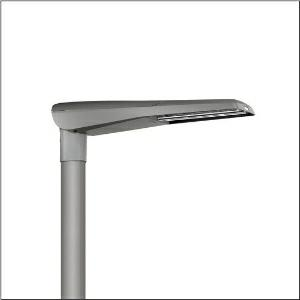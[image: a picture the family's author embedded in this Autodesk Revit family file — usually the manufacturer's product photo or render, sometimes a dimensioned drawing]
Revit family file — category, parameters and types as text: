
# Revit family: streetlight_sl_11_iq_mini___st0_5st0_5_5xc2hc1f08ge_9336
name_source: partatom
category: Lighting Fixtures
units: mm (PartAtom-declared; Revit-internal decimal feet)

## family parameters
Cut with Voids When Loaded = No
Host = Face
Light Source = No
Part Type = Normal
Room Calculation Point = No
Round Connector Dimension = Use Diameter
Shared = No

## types (1)
- --- (1 x LED, 3020 lm, 25.3 W, 2200K)
    Apparent Load = 25 VA
    CIE Flux Codes = 43 74 97 100 100
    Color Rendering = 70
    Color Temperature = 2200K
    Default Elevation = 1800 mm
    Description = Streetlight SL 11 iQ mini, mast luminaire, primary light control with 3 zone facetted reflector, of plastic, silver coated, highly specular, primary optical cover: cover, of PMMA, transparent, light distribution: ST0.5ST0.5, light emission: direct distribution, primary light characteristic: asymmetric, installation type: post-top, side-entry, lamps: LED, High Power LED, rated values: 3.550lm | 24,9W | 142,6lm/W (begin service life); end service life: 3.550lm | 25,7W; at 50% lumin. flux: 1.775lm | 12,8W | 138,7lm/W, colour temperature: 2200/2700/3000/4000K, colour rendering: CRI > 70, light colour: 722/727/730/740, light setting 1 begin service life: 100% | 3.550lm | 24,9W | 142,6lm/W | 3.000K, light setting 1 end service life: 25,7W, further light settings possible, control: Street-Remote, Auto-Match, Temp-Guard, Lumen-Switch, Night-Set, Smart-Wire, Light-Fading, Desk-Remote (wireless, voltage-free reading and setting of iQ features in the workshop via application-optimized NFC function/RFID function), optimised constant luminous flux control (CLO 2.0), with cable H07RN-F 5x 1.5mm², mains connection: 230..240V, AC, 50/60Hz, connection cable pre-assembled, cable length: 6,5m, luminaire housing, of diecast aluminium, powder-coated, Siteco® metallic grey (DB 702S), please order mast flange separately, inclination adjustable without tools: 0°, 5°, 10°, 15° (post-top) | 0°, -5°, -10°, -15° (side-entry), sealing non-destructively replaceable, multi-level sealing system, length: 736mm, width: 174mm, height: 116mm, mast flange for spigot size: 42mm (side-entry): 5XC10008XM4, 60/48mm (side-entry/post-top): 5XC10108XM2, 76/60mm (side-entry/post-top): 5XC10108XM1, equipment: standard, protection rating (complete): IP66, insulation class (complete): insulation class II (safety insulation), certification: CE, ENEC, ENEC+, VDE, impact resistance: IK10, permissible operating ambient temperature for outdoor applications: -25..+50°C, standard-compliant lighting for roads and squares, Environmental Product Declaration (EPD) tested and certified by an independent institute, packaging unit: 1 piece

Light Distribution: ST0.5ST0.5
    Height = 116 mm
    Lamp = 1 x LED
    Lamp Light Flux = 3020 lm
    Lamp Power = 25.3 W
    Lamp count = 1
    Length = 736 mm
    Luminous efficacy = 119 lm/W
    Manufacturer = Siteco
    ModVariant = No
    Model = 5XC2HC1F08GE
    Number of Poles = 1
    OnlyDefault = Yes
    Power Factor = 1
    Product Name = Streetlight SL 11 iQ mini | ST0.5ST0.5
    Product group = mast luminaire | pylon top
    ProductGroupID = 6100
    Protection Class = Protection class II
    Protection Degree = IP 66
    RLX_Detail_Level = 1
    RLX_Emergency_Light_Flux = 0 lm
    RLX_Emergency_Type = 0
    RLX_Emergency_Type_DB = No
    RlxData = <blob elided: 58005 chars, md5=56582fbc>
    Socket = socket
    Standby Power = 0 W
    System Light Flux = 3020 lm
    System Power = 25 W
    Type Comments = individual setting: luminous flux: 100 % | dim-lin: 254 | 351 mA
    Type Image = l_1003508.jpg
    URL = http://relux.com
    VarID = @adj_056127
    Voltage = 0 V
    Weight = 0.00 kg
    Width = 174 mm

## geometry (parser evidence)
native form markers: Blend x4, Sweep x11
no freeform markers — native parametric forms only
